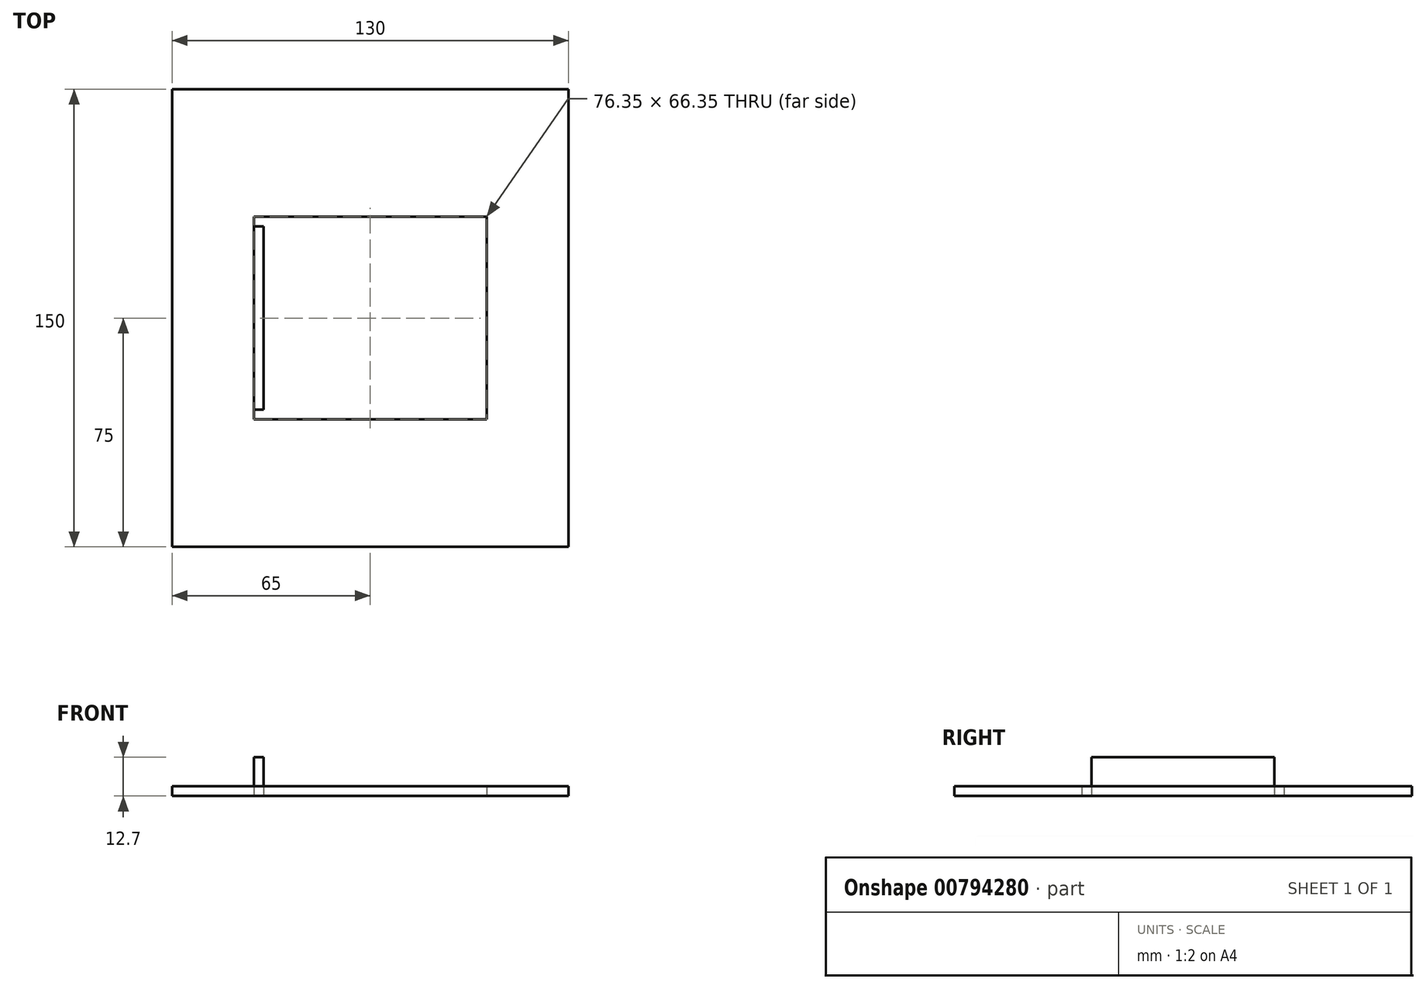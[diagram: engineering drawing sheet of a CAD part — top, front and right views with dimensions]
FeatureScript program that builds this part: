
annotation { "Feature Type Name" : "Feature", "Feature Type Description" : "" }
export const myFeature = defineFeature(function(context is Context, id is Id, definition is map)
    precondition{}
    {
        {
            var Q0;
            Q0=qCreatedBy(makeId("Top.planeOp"),FACE);
            var sketch = newSketch(context, id + "F0", { "sketchPlane" : qUnion([Q0])});
            skLineSegment(sketch, "E0.bottom", {"start": v(65, 75) * mm, "end": v(-65, 75) * mm});
            skLineSegment(sketch, "E0.top", {"start": v(65, -75) * mm, "end": v(-65, -75) * mm});
            skLineSegment(sketch, "E0.left", {"start": v(65, 75) * mm, "end": v(65, -75) * mm});
            skLineSegment(sketch, "E0.right", {"start": v(-65, 75) * mm, "end": v(-65, -75) * mm});
            skPoint(sketch, "E0.middle", {"position": v(0, 0) * mm});
            skLineSegment(sketch, "E1.bottom", {"start": v(35, 30) * mm, "end": v(-35, 30) * mm});
            skLineSegment(sketch, "E1.top", {"start": v(35, -30) * mm, "end": v(-35, -30) * mm});
            skLineSegment(sketch, "E1.left", {"start": v(35, 30) * mm, "end": v(35, -30) * mm});
            skLineSegment(sketch, "E1.right", {"start": v(-35, 30) * mm, "end": v(-35, -30) * mm});
            skLineSegment(sketch, "E2.0", {"start": v(38.17, 33.18) * mm, "end": v(-38.17, 33.18) * mm});
            skLineSegment(sketch, "E2.1", {"start": v(38.17, 33.18) * mm, "end": v(38.18, -33.17) * mm});
            skLineSegment(sketch, "E2.2", {"start": v(38.18, -33.17) * mm, "end": v(-38.17, -33.17) * mm});
            skLineSegment(sketch, "E2.3", {"start": v(-38.17, 33.18) * mm, "end": v(-38.17, -33.17) * mm});
            skLineSegment(sketch, "E3", {"start": v(-35, 30) * mm, "end": v(-38.17, 30) * mm});
            skLineSegment(sketch, "E4", {"start": v(35, 30) * mm, "end": v(38.17, 30) * mm});
            skLineSegment(sketch, "E5", {"start": v(35, -30) * mm, "end": v(38.18, -30) * mm});
            skLineSegment(sketch, "E6", {"start": v(-35, -30) * mm, "end": v(-38.17, -30) * mm});
            skSolve(sketch);
        }
        {
            var Q0;
            Q0=makeQuery(id+"F0.imprint","IMPRINT",FACE,{"disambiguationData":[TD([[makeQuery(id+"F0.imprint","IMPRINT",EDGE,{"derivedFrom":sQuery(id+"F0.wireOp",EDGE,"E0.bottom")}),1.0]])]});
            extrude(context, id + "F1", {"entities" : qUnion([Q0]), "depth" : 3.17 * mm, "offsetDistance" : 25.4 * mm});
        }
        {
            var Q0;
            Q0=makeQuery(id+"F0.imprint","IMPRINT",FACE,{"disambiguationData":[TD([[makeQuery(id+"F0.imprint","IMPRINT",EDGE,{"derivedFrom":sQuery(id+"F0.wireOp",EDGE,"E1.right")}),-1.0]])]});
            extrude(context, id + "F2", {"entities" : qUnion([Q0]), "depth" : 12.7 * mm, "offsetDistance" : 25.4 * mm});
        }
    });
